# Revit family: Hager-Univers-IP65-D300-H850-Cl.II-encl-NoHosted-PL-pl
name_source: partatom
category: Equipement électrique
units: mm (PartAtom-declared; Revit-internal decimal feet)

## family parameters
Basée sur le plan de construction = Oui
Configuration du panneau = Deux colonnes, circuits au sein
Cote de connecteur circulaire = Utiliser le diamètre
Couper avec des vides une fois chargée = Non
Partagée = Non
Point de calcul de pièce = Non
Toujours verticalement = Oui
Type d'élément = Tableau de raccordement

## types (6) — shared parameters
Commentaires du type = Univers
EF000003 - Sposób montażu = EV000384 - Montaż natynkowy
EF000007 - Kolor = EV000270 - Szary
EF000040 - Wysokość = 850 mm  [stored 2.78871 ft]
EF000049 - Głębokość = 300 mm  [stored 0.984252 ft]
EF000116 - Numer RAL = 7035
EF000118 - Z płytą montażową = Non
EF000266 - Liczba rzędów = 5
EF001088 - Możliwość rozbudowy = Non
EF001596 - Materiał obudowy = EV000139 - Tworzywo sztuczne
EF001613 - Podtrzymanie funkcji = EV000494 - Brak
EF003532 - Do zastosowań zewnętrznych = Oui
EF004293 - Odporność udarowa = EV008784 - IK10
EF004464 - Rodzaj drzwi = EV002646 - Pojedynczy
EF005474 - Stopień ochrony (IP) = EV006421 - IP65
EF006244 - Transparentna pokrywa/drzwi = Non
EF006306 - Z zamkiem = Oui
EF007800 - Do ochrony odgromowej = Oui
EF009170 - Obudowa z materiału o wysokiej wytrzymałości mechanicznej = 2 mm  [stored 0.00656168 ft]
EF009171 - Drzwi/pokrywa z materiału o wysokiej wytrzymałości mechanicznej = 2 mm  [stored 0.00656168 ft]
EF009212 - Wykonanie pokrywy = EV000116 - Zamknięty
EF015940 - Pokrywa z wyzwalaczem nadciśnieniowym = Non
Elévation par défaut = 1219 mm
Fabricant = Hager
HG000002 - Z drzwiami lub pokrywą = Oui
HG000003 - Zakres = Univers
HG000006 - Montaż podtynkowy = Non
HG000009 - Drzwi dwuskrzydłowe = Non
HG000010 - Drzwi asymetryczne = Non
HG000023 - Obudowa dwusekcyjna = Non
HG000024 - Wysokość części dolnej = 600 mm
HG000026 - Stojąca = Non
zero-valued in all types: EF000218 - Głębokość wbudowania, EF000437 - Liczba wejść kablowych, EF009554 - Liczba otworów pod flansze, HG000027 - Wysokość cokołu

## per-type parameters (varying)
| type | EF000008 - Szerokość | EF000339 - Rodzaj pokrywy | EF001131 - Głębokość wewnętrzna | EF002950 - Szerokość wyrażona liczbą modułów | EF004427 - Liczba modułów | EF008873 - Prąd znamionowy (In) | HG000004 - Referencja producenta |
| Montaż natynkowy IP65 S1100 W850 G300  - FL54S | 1100 mm | EV004216 - Drzwi | 150 mm  [stored 0.492126 ft] | 48 | 240 | 630 A | FL54S |
| Montaż natynkowy IP65 S1100 W850 G300  - FL54SP | 1100 mm | EV004216 - Drzwi | 150 mm  [stored 0.492126 ft] | 48 | 240 | 630 A | FL54SP |
| Montaż natynkowy IP65 S600 W850 G300  - FL52S | 600 mm | EV004216 - Drzwi | 235 mm  [stored 0.770997 ft] | 24 | 120 | 630 A | FL52S |
| Montaż natynkowy IP65 S600 W850 G300  - FL52SP | 600 mm | EV004216 - Drzwi | 235 mm  [stored 0.770997 ft] | 24 | 120 | 400 A | FL52SP |
| Montaż natynkowy IP65 S850 W850 G300  - FL53S | 850 mm  [stored 2.78871 ft] | EV001012 - Pokrywa | 150 mm  [stored 0.492126 ft] | 36 | 180 | 400 A | FL53S |
| Montaż natynkowy IP65 S850 W850 G300  - FL53SP | 850 mm  [stored 2.78871 ft] | EV001012 - Pokrywa | 150 mm  [stored 0.492126 ft] | 36 | 180 | 400 A | FL53SP |

note: [stored X ft] marks values corroborated as IEEE doubles in the binary element streams (Revit-internal decimal feet)

## geometry (parser evidence)
native form markers: Blend x4, Sweep x6
no freeform markers — native parametric forms only
